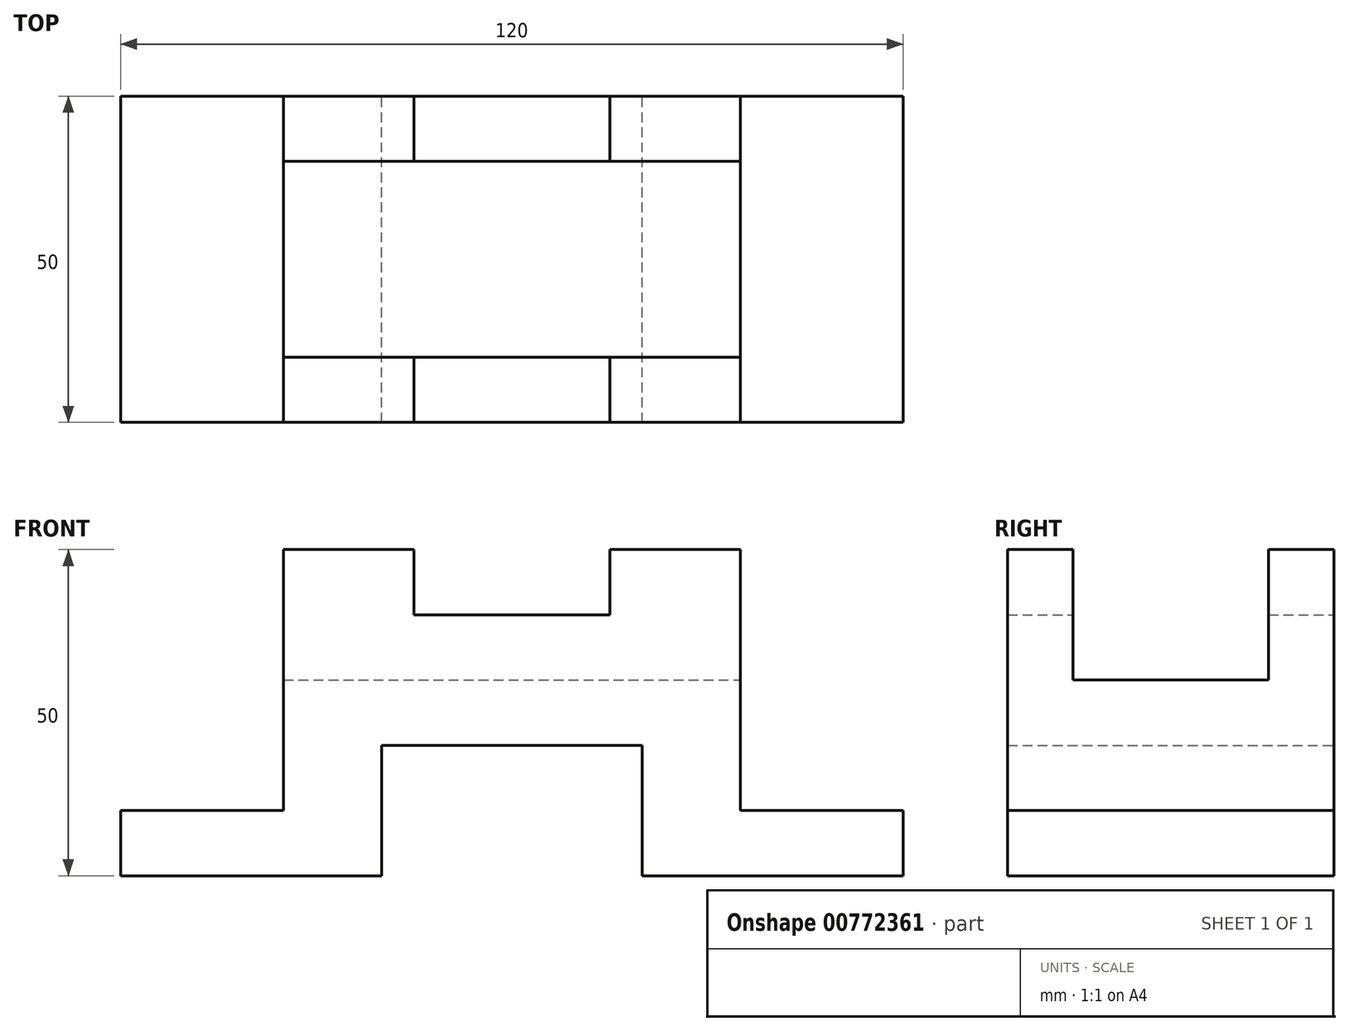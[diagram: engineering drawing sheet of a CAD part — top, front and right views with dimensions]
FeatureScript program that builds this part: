
annotation { "Feature Type Name" : "Feature", "Feature Type Description" : "" }
export const myFeature = defineFeature(function(context is Context, id is Id, definition is map)
    precondition{}
    {
        {
            var Q0;
            Q0=qCreatedBy(makeId("Front.planeOp"),FACE);
            var sketch = newSketch(context, id + "F0", { "sketchPlane" : qUnion([Q0])});
            skLineSegment(sketch, "E0", {"start": v(20, 0) * mm, "end": v(-20, 0) * mm});
            skLineSegment(sketch, "E1", {"start": v(-20, 0) * mm, "end": v(-20, -20) * mm});
            skLineSegment(sketch, "E2", {"start": v(-20, -20) * mm, "end": v(-60, -20) * mm});
            skLineSegment(sketch, "E3", {"start": v(-60, -20) * mm, "end": v(-60, -10) * mm});
            skLineSegment(sketch, "E4", {"start": v(-60, -10) * mm, "end": v(-35, -10) * mm});
            skLineSegment(sketch, "E5", {"start": v(-35, -10) * mm, "end": v(-35, 30) * mm});
            skLineSegment(sketch, "E6", {"start": v(-35, 30) * mm, "end": v(-15, 30) * mm});
            skLineSegment(sketch, "E7", {"start": v(-15, 30) * mm, "end": v(-15, 20) * mm});
            skLineSegment(sketch, "E8", {"start": v(-15, 20) * mm, "end": v(15, 20) * mm});
            skLineSegment(sketch, "E9", {"start": v(15, 20) * mm, "end": v(15, 30) * mm});
            skLineSegment(sketch, "E10", {"start": v(15, 30) * mm, "end": v(35, 30) * mm});
            skLineSegment(sketch, "E11", {"start": v(35, 30) * mm, "end": v(35, -10) * mm});
            skLineSegment(sketch, "E12", {"start": v(35, -10) * mm, "end": v(60, -10) * mm});
            skLineSegment(sketch, "E13", {"start": v(60, -10) * mm, "end": v(60, -20) * mm});
            skLineSegment(sketch, "E14", {"start": v(60, -20) * mm, "end": v(20, -20) * mm});
            skLineSegment(sketch, "E15", {"start": v(20, -20) * mm, "end": v(20, 0) * mm});
            skLineSegment(sketch, "E16", {"start": v(-35, 10) * mm, "end": v(35, 10) * mm});
            skSolve(sketch);
        }
        {
            var Q0;
            Q0 = qSketchRegion(id + "F0", true);
            extrude(context, id + "F1", {"entities" : qUnion([Q0]), "endBound" : BoundingType.SYMMETRIC, "depth" : 50 * mm, "offsetDistance" : 25 * mm});
        }
        {
            var Q0;
            {var subQ0=sQuery(id+"F0.wireOp",EDGE,"E6");Q0=makeQuery(id+"F0.imprint","IMPRINT",FACE,{"disambiguationData":[TD([[makeQuery(id+"F0.imprint","IMPRINT",EDGE,{"derivedFrom":subQ0}),-1.0]])]});}
            extrude(context, id + "F2", {"entities" : qUnion([Q0]), "operationType" : NewBodyOperationType.REMOVE, "endBound" : BoundingType.SYMMETRIC, "oppositeDirection" : true, "depth" : 30 * mm, "offsetDistance" : 25 * mm});
        }
    });
